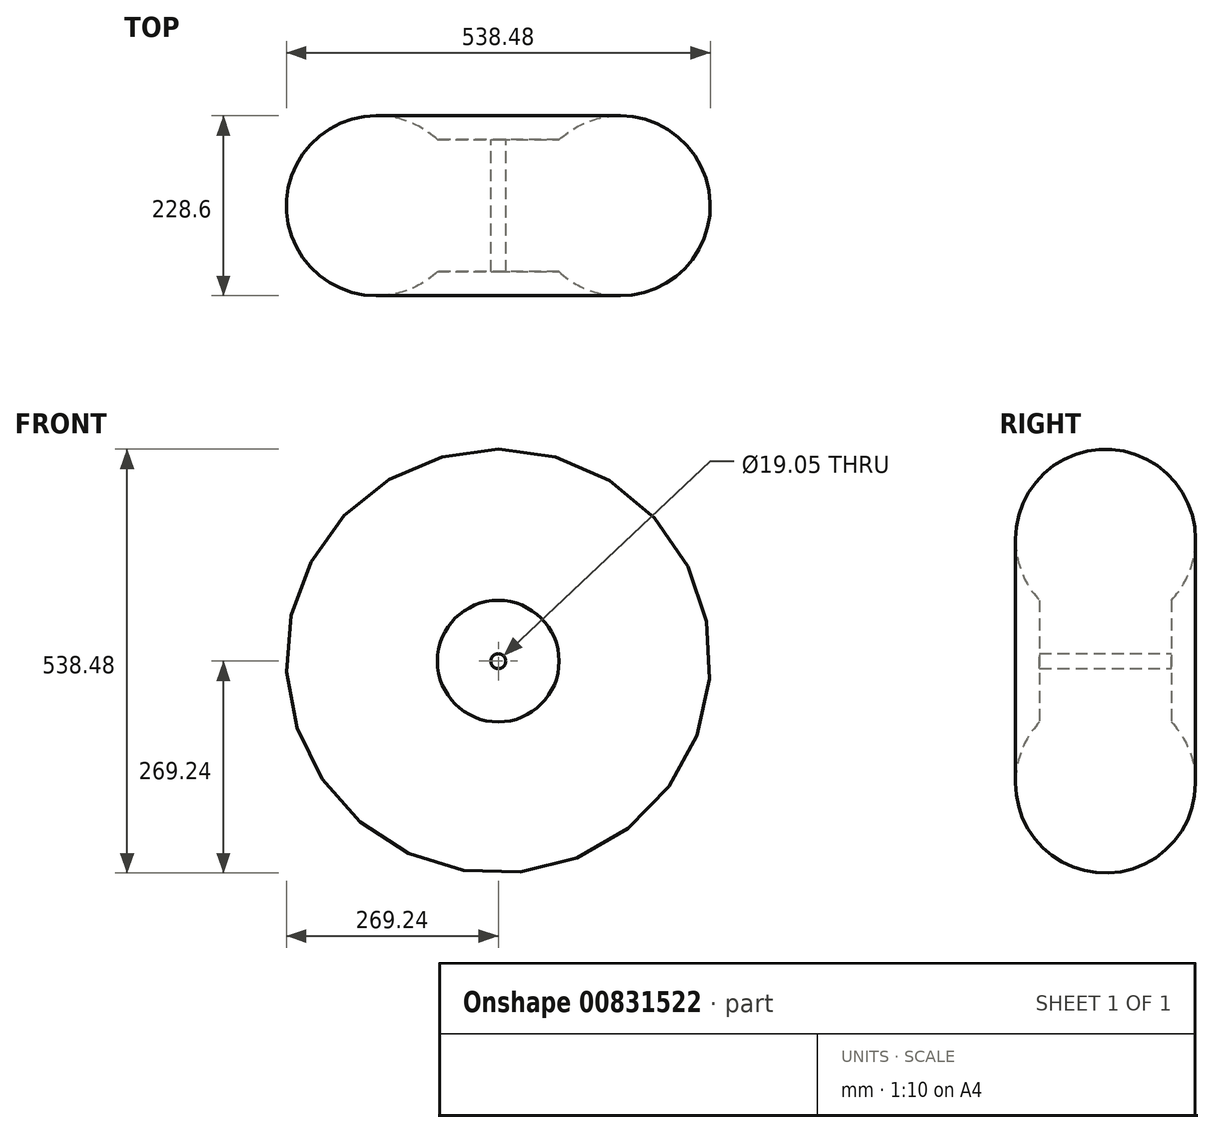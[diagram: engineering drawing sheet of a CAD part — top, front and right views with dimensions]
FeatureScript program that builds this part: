
annotation { "Feature Type Name" : "Feature", "Feature Type Description" : "" }
export const myFeature = defineFeature(function(context is Context, id is Id, definition is map)
    precondition{}
    {
        {
            var Q0;
            Q0=qCreatedBy(makeId("Front.planeOp"),FACE);
            var sketch = newSketch(context, id + "F0", { "sketchPlane" : qUnion([Q0])});
            skCircle(sketch, "E0", {"center": v(0, 0) * mm, "radius": 243.84 * mm, "construction": true});
            skCircle(sketch, "E1", {"center": v(0, 0) * mm, "radius": 88.9 * mm, "construction": true});
            skCircle(sketch, "E2", {"center": v(0, 0) * mm, "radius": 166.37 * mm});
            skSolve(sketch);
        }
        {
            var Q0;
            Q0=qCreatedBy(makeId("Top.planeOp"),FACE);
            var sketch = newSketch(context, id + "F1", { "sketchPlane" : qUnion([Q0])});
            skCircle(sketch, "E3", {"center": v(154.94, 0) * mm, "radius": 114.3 * mm});
            skSolve(sketch);
        }
        {
            var Q0;
            Q0=makeQuery(id+"F1.imprint","IMPRINT",FACE,{"disambiguationData":[TD([[makeQuery(id+"F1.imprint","IMPRINT",EDGE,{"derivedFrom":sQuery(id+"F1.wireOp",EDGE,"E3")}),1.0]])]});
            var Q1;
            Q1=sQuery(id+"F0.wireOp",EDGE,"E2");
            sweep(context, id + "F2", {"profiles" : qUnion([Q0]), "path" : qUnion([Q1])});
        }
        {
            var Q0;
            Q0=qCreatedBy(makeId("Front.planeOp"),FACE);
            var sketch = newSketch(context, id + "F3", { "sketchPlane" : qUnion([Q0])});
            skCircle(sketch, "E4", {"center": v(0, 0) * mm, "radius": 88.9 * mm});
            skCircle(sketch, "E5", {"center": v(0, 0) * mm, "radius": 9.53 * mm});
            skSolve(sketch);
        }
        {
            var Q0;
            Q0 = qSketchRegion(id + "F3", true);
            extrude(context, id + "F4", {"entities" : qUnion([Q0]), "operationType" : NewBodyOperationType.ADD, "depth" : 83.82 * mm, "offsetDistance" : 25.4 * mm, "hasSecondDirection" : true, "secondDirectionOppositeDirection" : true, "secondDirectionDepth" : 83.82 * mm});
        }
    });
